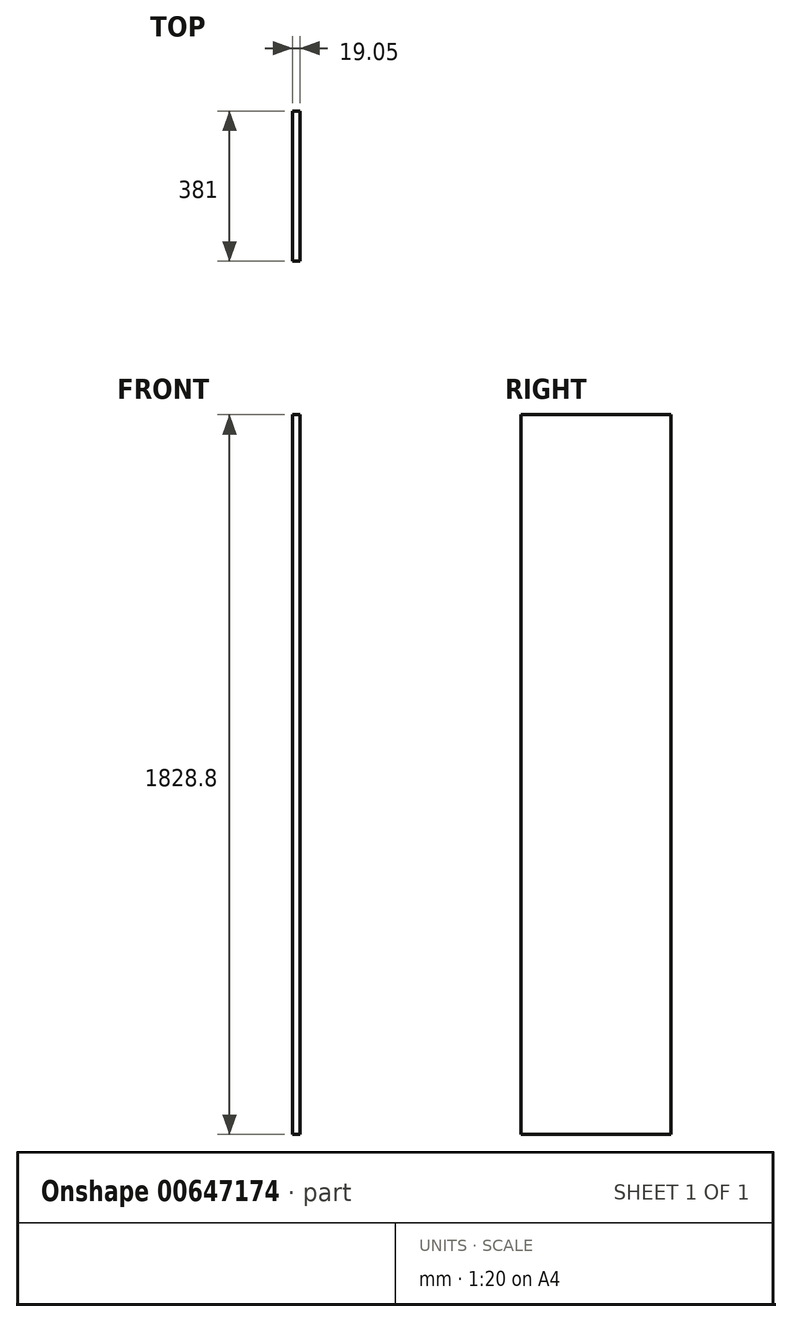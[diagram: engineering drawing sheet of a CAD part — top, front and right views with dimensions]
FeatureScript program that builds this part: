
annotation { "Feature Type Name" : "Feature", "Feature Type Description" : "" }
export const myFeature = defineFeature(function(context is Context, id is Id, definition is map)
    precondition{}
    {
        {
            var Q0;
            Q0=qCreatedBy(makeId("Right.planeOp"),FACE);
            var sketch = newSketch(context, id + "F0", { "sketchPlane" : qUnion([Q0])});
            skLineSegment(sketch, "E0.bottom", {"start": v(190.5, 914.4) * mm, "end": v(-190.5, 914.4) * mm});
            skLineSegment(sketch, "E0.top", {"start": v(190.5, -914.4) * mm, "end": v(-190.5, -914.4) * mm});
            skLineSegment(sketch, "E0.left", {"start": v(190.5, 914.4) * mm, "end": v(190.5, -914.4) * mm});
            skLineSegment(sketch, "E0.right", {"start": v(-190.5, 914.4) * mm, "end": v(-190.5, -914.4) * mm});
            skPoint(sketch, "E0.middle", {"position": v(0, 0) * mm});
            skSolve(sketch);
        }
        {
            var Q0;
            Q0=makeQuery(id+"F0.imprint","IMPRINT",FACE,{"disambiguationData":[TD([[makeQuery(id+"F0.imprint","IMPRINT",EDGE,{"derivedFrom":sQuery(id+"F0.wireOp",EDGE,"E0.bottom")}),1.0]])]});
            extrude(context, id + "F1", {"entities" : qUnion([Q0]), "depth" : 19.05 * mm, "offsetDistance" : 25.4 * mm});
        }
    });
